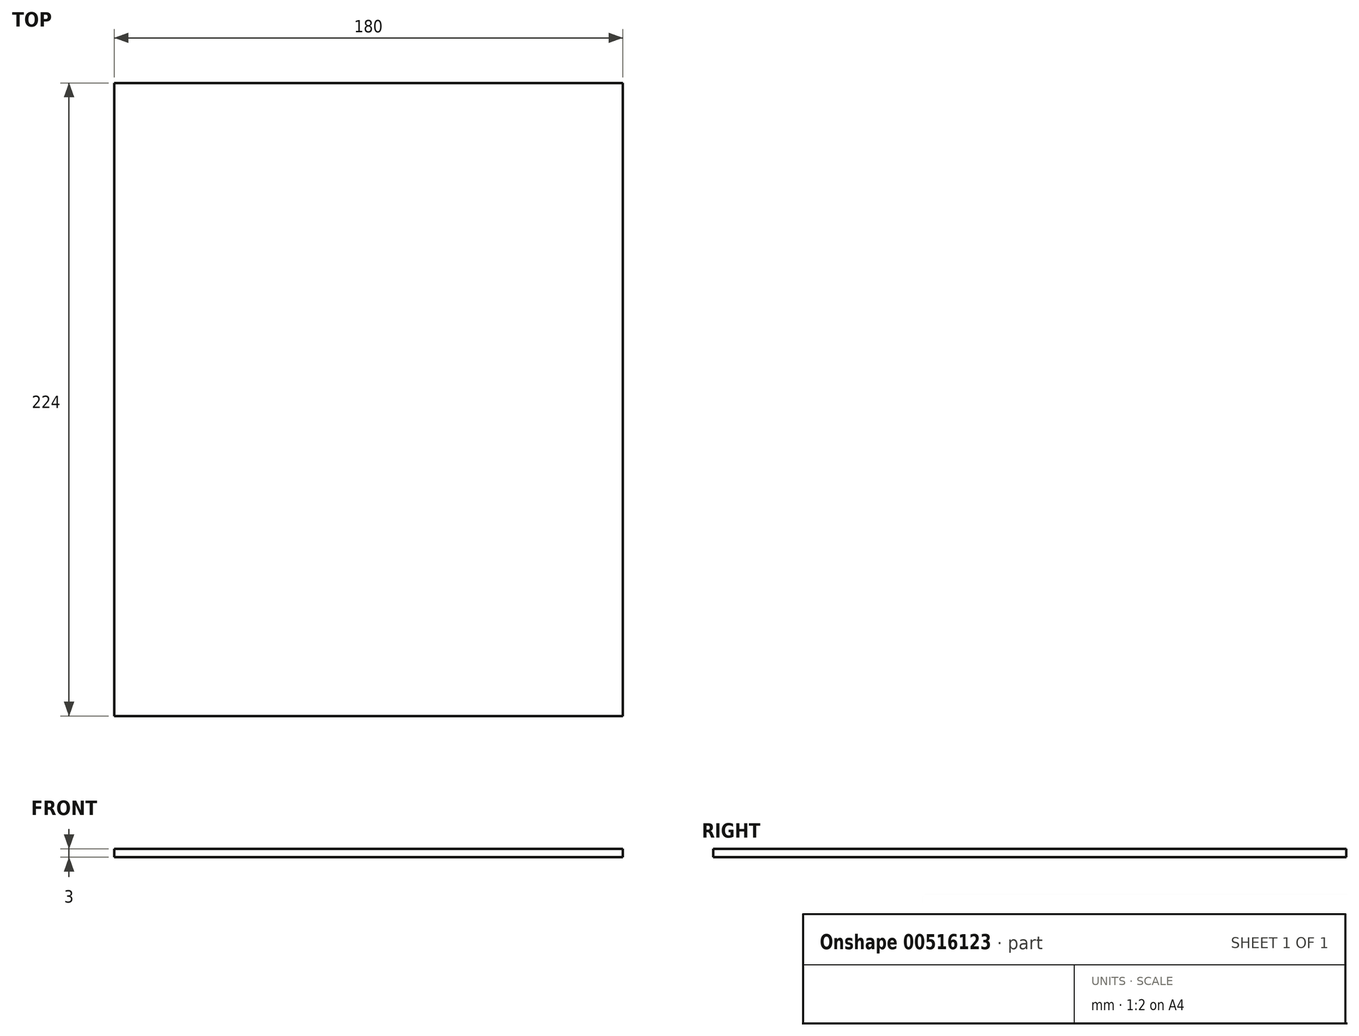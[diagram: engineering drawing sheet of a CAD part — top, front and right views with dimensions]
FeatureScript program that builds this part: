
annotation { "Feature Type Name" : "Feature", "Feature Type Description" : "" }
export const myFeature = defineFeature(function(context is Context, id is Id, definition is map)
    precondition{}
    {
        {
            var Q0;
            Q0=qCreatedBy(makeId("Top.planeOp"),FACE);
            var sketch = newSketch(context, id + "F0", { "sketchPlane" : qUnion([Q0])});
            skLineSegment(sketch, "E0", {"start": v(0, 0) * mm, "end": v(0, 224) * mm});
            skLineSegment(sketch, "E1", {"start": v(0, 224) * mm, "end": v(180, 224) * mm});
            skLineSegment(sketch, "E2", {"start": v(180, 224) * mm, "end": v(180, 0) * mm});
            skLineSegment(sketch, "E3", {"start": v(180, 0) * mm, "end": v(0, 0) * mm});
            skSolve(sketch);
        }
        {
            var Q0;
            Q0=makeQuery(id+"F0.imprint","IMPRINT",FACE,{"disambiguationData":[TD([[makeQuery(id+"F0.imprint","IMPRINT",EDGE,{"derivedFrom":sQuery(id+"F0.wireOp",EDGE,"E0")}),-1.0]])]});
            extrude(context, id + "F1", {"entities" : qUnion([Q0]), "depth" : 3 * mm, "offsetDistance" : 25 * mm});
        }
    });
